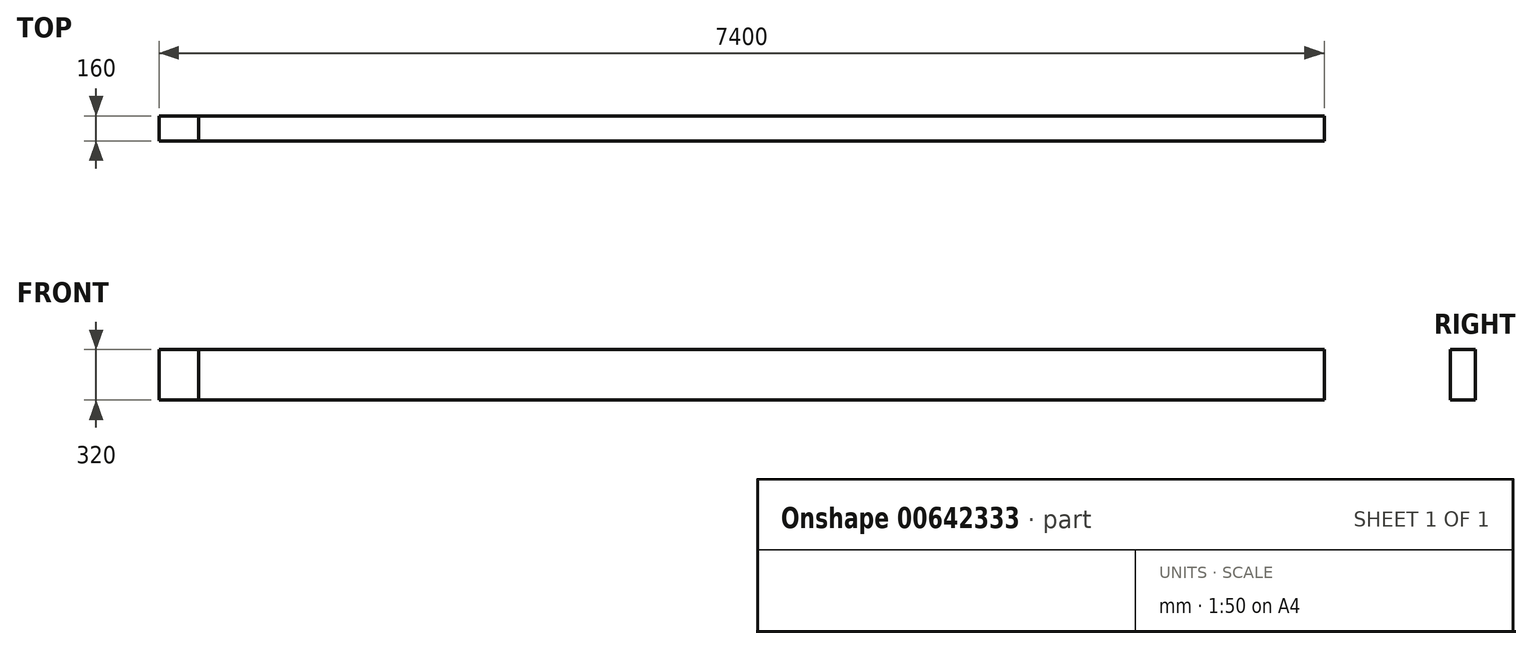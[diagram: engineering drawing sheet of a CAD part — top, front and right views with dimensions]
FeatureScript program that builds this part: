
annotation { "Feature Type Name" : "Feature", "Feature Type Description" : "" }
export const myFeature = defineFeature(function(context is Context, id is Id, definition is map)
    precondition{}
    {
        {
            var Q0;
            Q0=qCreatedBy(makeId("Right.planeOp"),FACE);
            var sketch = newSketch(context, id + "F0", { "sketchPlane" : qUnion([Q0])});
            skLineSegment(sketch, "E0.bottom", {"start": v(80, 160) * mm, "end": v(-80, 160) * mm});
            skLineSegment(sketch, "E0.top", {"start": v(80, -160) * mm, "end": v(-80, -160) * mm});
            skLineSegment(sketch, "E0.left", {"start": v(80, 160) * mm, "end": v(80, -160) * mm});
            skLineSegment(sketch, "E0.right", {"start": v(-80, 160) * mm, "end": v(-80, -160) * mm});
            skPoint(sketch, "E0.middle", {"position": v(0, 0) * mm});
            skLineSegment(sketch, "E1", {"start": v(-80, 0) * mm, "end": v(80, 0) * mm});
            skSolve(sketch);
        }
        {
            var Q0;
            {var subQ0=sQuery(id+"F0.wireOp",EDGE,"E0.bottom");Q0=makeQuery(id+"F0.imprint","IMPRINT",FACE,{"disambiguationData":[TD([[makeQuery(id+"F0.imprint","IMPRINT",EDGE,{"derivedFrom":subQ0}),1.0]])]});}
            var Q1;
            {var subQ0=sQuery(id+"F0.wireOp",EDGE,"E0.top");Q1=makeQuery(id+"F0.imprint","IMPRINT",FACE,{"disambiguationData":[TD([[makeQuery(id+"F0.imprint","IMPRINT",EDGE,{"derivedFrom":subQ0}),-1.0]])]});}
            extrude(context, id + "F1", {"entities" : qUnion([Q0, Q1]), "depth" : 7400 * mm, "offsetDistance" : 25 * mm});
        }
        {
            var Q0;
            {var subQ0=sQuery(id+"F0.wireOp",EDGE,"E0.bottom");Q0=makeQuery(id+"F0.imprint","IMPRINT",FACE,{"disambiguationData":[TD([[makeQuery(id+"F0.imprint","IMPRINT",EDGE,{"derivedFrom":subQ0}),1.0]])]});}
            var Q1;
            {var subQ0=sQuery(id+"F0.wireOp",EDGE,"E0.top");Q1=makeQuery(id+"F0.imprint","IMPRINT",FACE,{"disambiguationData":[TD([[makeQuery(id+"F0.imprint","IMPRINT",EDGE,{"derivedFrom":subQ0}),-1.0]])]});}
            extrude(context, id + "F2", {"entities" : qUnion([Q0, Q1]), "depth" : 250 * mm, "offsetDistance" : 25 * mm});
        }
    });
